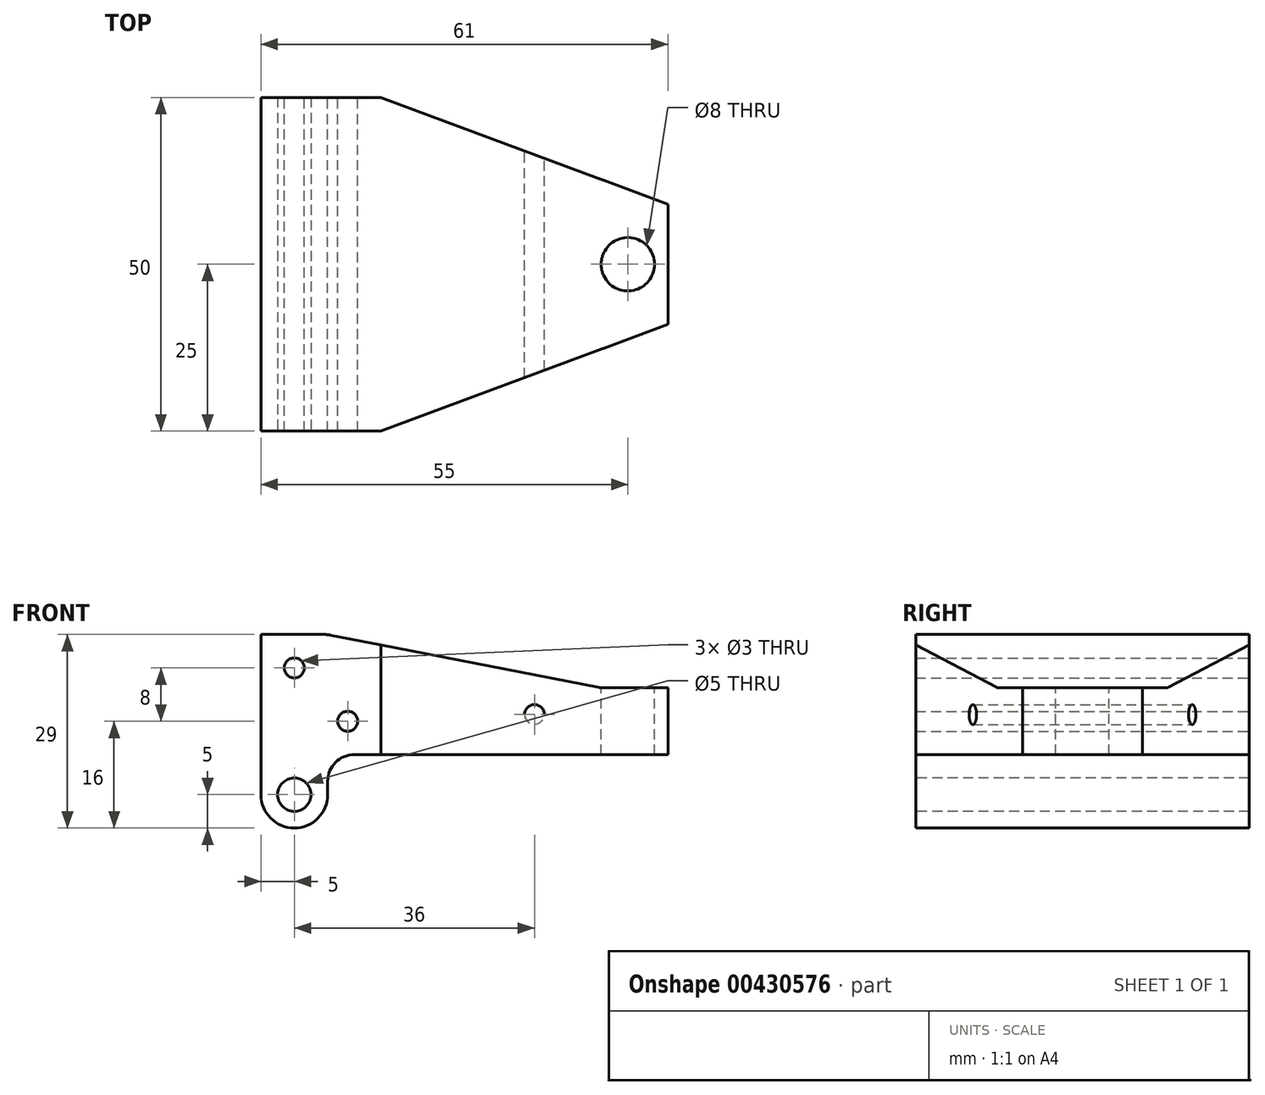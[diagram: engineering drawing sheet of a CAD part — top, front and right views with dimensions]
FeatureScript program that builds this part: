
annotation { "Feature Type Name" : "Feature", "Feature Type Description" : "" }
export const myFeature = defineFeature(function(context is Context, id is Id, definition is map)
    precondition{}
    {
        {
            var Q0;
            Q0=qCreatedBy(makeId("Front.planeOp"),FACE);
            var sketch = newSketch(context, id + "F0", { "sketchPlane" : qUnion([Q0])});
            skLineSegment(sketch, "E0", {"start": v(-5, 24) * mm, "end": v(5, 24) * mm});
            skLineSegment(sketch, "E1", {"start": v(5, 24) * mm, "end": v(46, 16) * mm});
            skLineSegment(sketch, "E2", {"start": v(46, 16) * mm, "end": v(56, 16) * mm});
            skLineSegment(sketch, "E3", {"start": v(56, 16) * mm, "end": v(56, 6) * mm});
            skLineSegment(sketch, "E4", {"start": v(56, 6) * mm, "end": v(5, 6) * mm});
            skLineSegment(sketch, "E5", {"start": v(5, 6) * mm, "end": v(5, 0) * mm});
            skArc(sketch, "E6", {"start": v(-5, 0) * mm, "mid": v(0, -5) * mm, "end": v(5, 0) * mm});
            skLineSegment(sketch, "E7.trimOffspring", {"start": v(-5, 0) * mm, "end": v(-5, 24) * mm});
            skCircle(sketch, "E8", {"center": v(0, 19) * mm, "radius": 1.5 * mm});
            skCircle(sketch, "E9", {"center": v(8, 11) * mm, "radius": 1.5 * mm});
            skCircle(sketch, "E10", {"center": v(36, 12) * mm, "radius": 1.5 * mm});
            skSolve(sketch);
        }
        {
            var Q0;
            Q0 = qSketchRegion(id + "F0", true);
            extrude(context, id + "F1", {"entities" : qUnion([Q0]), "endBound" : BoundingType.SYMMETRIC, "depth" : 50 * mm, "offsetDistance" : 25 * mm});
        }
        {
            var Q0;
            Q0=makeQuery(id+"F1.opExtrude","CAP_FACE",FACE,{"disambiguationData":[OSD([sQuery(id+"F0.wireOp",EDGE,"wXhLJt5r-CjcR-nyDZ-la2q-2bztBm83fng6"),sQuery(id+"F0.wireOp",EDGE,"E0"),sQuery(id+"F0.wireOp",EDGE,"E1"),sQuery(id+"F0.wireOp",EDGE,"E2"),sQuery(id+"F0.wireOp",EDGE,"E3"),sQuery(id+"F0.wireOp",EDGE,"E4"),sQuery(id+"F0.wireOp",EDGE,"E5"),sQuery(id+"F0.wireOp",EDGE,"E6"),sQuery(id+"F0.wireOp",EDGE,"KROrUDzY-2ixT-Jzr4-ytVV-uIM1JRgbrqm2.bottom"),sQuery(id+"F0.wireOp",EDGE,"KROrUDzY-2ixT-Jzr4-ytVV-uIM1JRgbrqm2.top"),sQuery(id+"F0.wireOp",EDGE,"KROrUDzY-2ixT-Jzr4-ytVV-uIM1JRgbrqm2.right"),sQuery(id+"F0.wireOp",EDGE,"E7.trimOffspring")])],"isStart":false});
            var sketch = newSketch(context, id + "F2", { "sketchPlane" : qUnion([Q0])});
            skPoint(sketch, "E11", {"position": v(0, 0) * mm});
            skSolve(sketch);
        }
        {
            var Q0;
            Q0=sQuery(id+"F2.wireOp",VERTEX,"E11");
            var Q1;
            Q1=makeQuery(id+"F1.opExtrude","SWEPT_BODY",BODY,{"disambiguationData":[OSD([sQuery(id+"F0.wireOp",EDGE,"wXhLJt5r-CjcR-nyDZ-la2q-2bztBm83fng6"),sQuery(id+"F0.wireOp",EDGE,"E0"),sQuery(id+"F0.wireOp",EDGE,"E1"),sQuery(id+"F0.wireOp",EDGE,"E2"),sQuery(id+"F0.wireOp",EDGE,"E3"),sQuery(id+"F0.wireOp",EDGE,"E4"),sQuery(id+"F0.wireOp",EDGE,"E5"),sQuery(id+"F0.wireOp",EDGE,"E6"),sQuery(id+"F0.wireOp",EDGE,"KROrUDzY-2ixT-Jzr4-ytVV-uIM1JRgbrqm2.bottom"),sQuery(id+"F0.wireOp",EDGE,"KROrUDzY-2ixT-Jzr4-ytVV-uIM1JRgbrqm2.top"),sQuery(id+"F0.wireOp",EDGE,"KROrUDzY-2ixT-Jzr4-ytVV-uIM1JRgbrqm2.right"),sQuery(id+"F0.wireOp",EDGE,"E7.trimOffspring"),sQuery(id+"F0.wireOp",EDGE,"E8"),sQuery(id+"F0.wireOp",EDGE,"E9")])]});
            hole(context, id + "F3", {"style" : HoleStyle.SIMPLE, "endStyle" : HoleEndStyle.THROUGH, "holeDiameter" : 5 * mm, "isTappedThrough" : true, "tappedDepth" : 12 * mm, "tapClearance" : 3, "locations" : qUnion([Q0]), "scope" : qUnion([Q1])});
        }
        {
            var Q0;
            Q0=makeQuery(id+"F1.opExtrude","SWEPT_EDGE",EDGE,{"disambiguationData":[OSD([sQuery(id+"F0.wireOp",EDGE,"E4"),sQuery(id+"F0.wireOp",EDGE,"E5")])]});
            var Q1;
            Q1=makeQuery(id+"F1.opExtrude","SWEPT_EDGE",EDGE,{"disambiguationData":[OSD([sQuery(id+"F0.wireOp",EDGE,"E0"),sQuery(id+"F0.wireOp",EDGE,"E1")])]});
            var Q2;
            Q2=makeQuery(id+"F1.opExtrude","SWEPT_EDGE",EDGE,{"disambiguationData":[OSD([sQuery(id+"F0.wireOp",EDGE,"E1"),sQuery(id+"F0.wireOp",EDGE,"E2")])]});
            fillet(context, id + "F4", {"entities" : qUnion([Q0, Q1, Q2]), "radius" : 4 * mm, "tangentPropagation" : true, "allowEdgeOverflow" : false});
        }
        {
            var Q0;
            Q0=makeQuery(id+"F1.opExtrude","SWEPT_FACE",FACE,{"disambiguationData":[OSD([sQuery(id+"F0.wireOp",EDGE,"E0")])]});
            var sketch = newSketch(context, id + "F5", { "sketchPlane" : qUnion([Q0])});
            skPoint(sketch, "E12", {"position": v(50, 0) * mm});
            skSolve(sketch);
        }
        {
            var Q0;
            Q0=sQuery(id+"F5.wireOp",VERTEX,"E12");
            var Q1;
            Q1=makeQuery(id+"F1.opExtrude","SWEPT_BODY",BODY,{"disambiguationData":[OSD([sQuery(id+"F0.wireOp",EDGE,"wXhLJt5r-CjcR-nyDZ-la2q-2bztBm83fng6"),sQuery(id+"F0.wireOp",EDGE,"E0"),sQuery(id+"F0.wireOp",EDGE,"E1"),sQuery(id+"F0.wireOp",EDGE,"E2"),sQuery(id+"F0.wireOp",EDGE,"E3"),sQuery(id+"F0.wireOp",EDGE,"E4"),sQuery(id+"F0.wireOp",EDGE,"E5"),sQuery(id+"F0.wireOp",EDGE,"E6"),sQuery(id+"F0.wireOp",EDGE,"KROrUDzY-2ixT-Jzr4-ytVV-uIM1JRgbrqm2.bottom"),sQuery(id+"F0.wireOp",EDGE,"KROrUDzY-2ixT-Jzr4-ytVV-uIM1JRgbrqm2.top"),sQuery(id+"F0.wireOp",EDGE,"KROrUDzY-2ixT-Jzr4-ytVV-uIM1JRgbrqm2.right"),sQuery(id+"F0.wireOp",EDGE,"E7.trimOffspring"),sQuery(id+"F0.wireOp",EDGE,"E8"),sQuery(id+"F0.wireOp",EDGE,"E9")])]});
            hole(context, id + "F6", {"style" : HoleStyle.SIMPLE, "endStyle" : HoleEndStyle.THROUGH, "holeDiameter" : 8 * mm, "isTappedThrough" : true, "tappedDepth" : 12 * mm, "tapClearance" : 3, "locations" : qUnion([Q0]), "scope" : qUnion([Q1])});
        }
        {
            var Q0;
            Q0=makeQuery(id+"F1.opExtrude","SWEPT_FACE",FACE,{"disambiguationData":[OSD([sQuery(id+"F0.wireOp",EDGE,"E0")])]});
            var sketch = newSketch(context, id + "F7", { "sketchPlane" : qUnion([Q0])});
            skLineSegment(sketch, "E13", {"start": v(13, 25) * mm, "end": v(56, 9) * mm});
            skLineSegment(sketch, "E14.MirrorCS", {"start": v(13, -25) * mm, "end": v(56, -9) * mm});
            skLineSegment(sketch, "E15", {"start": v(56, 9) * mm, "end": v(56, -9) * mm});
            skLineSegment(sketch, "E16", {"start": v(13, 25) * mm, "end": v(13, 45) * mm});
            skLineSegment(sketch, "E17", {"start": v(13, 45) * mm, "end": v(76, 45) * mm});
            skLineSegment(sketch, "E18", {"start": v(76, 45) * mm, "end": v(76, -45) * mm});
            skLineSegment(sketch, "E19", {"start": v(76, -45) * mm, "end": v(13, -45) * mm});
            skLineSegment(sketch, "E20", {"start": v(13, -45) * mm, "end": v(13, -25) * mm});
            skSolve(sketch);
        }
        {
            var Q0;
            Q0=makeQuery(id+"F7.imprint","IMPRINT",FACE,{"disambiguationData":[TD([[makeQuery(id+"F7.imprint","IMPRINT",EDGE,{"derivedFrom":sQuery(id+"F7.wireOp",EDGE,"E13")}),1.0]])]});
            extrude(context, id + "F8", {"entities" : qUnion([Q0]), "operationType" : NewBodyOperationType.REMOVE, "endBound" : BoundingType.THROUGH_ALL, "oppositeDirection" : true, "depth" : 25 * mm, "offsetDistance" : 25 * mm});
        }
    });
